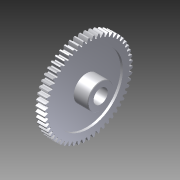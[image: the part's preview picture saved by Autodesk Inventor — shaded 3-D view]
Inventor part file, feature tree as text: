
AUTODESK INVENTOR PART (.ipt)
format: ipt  version: 2012 (Build 160160000, 160)  size: 1,032,704 bytes
history: native  units: in
note: dims shown in document units (in); Inventor stores cm internally (conversion verified against a paired STEP export)
features: sketch x1, extrude x1, imported_body x1
ambient origin geometry x8: Origin, YZ Plane, XZ Plane, XY Plane, X Axis, Y Axis, Z Axis, Center Point
feature tree (3):
  sketch  "Sketch1"  dims[d0=0.375in d3=0.3in d4=0.0in d5=1.0in d6=0.125in d7=0.125in d8=0.0625in d9=0.5625in]
  extrude  "Extrusion2"  Depth=0.3in TaperAngle=0.0deg
  imported_body  "Base1"
